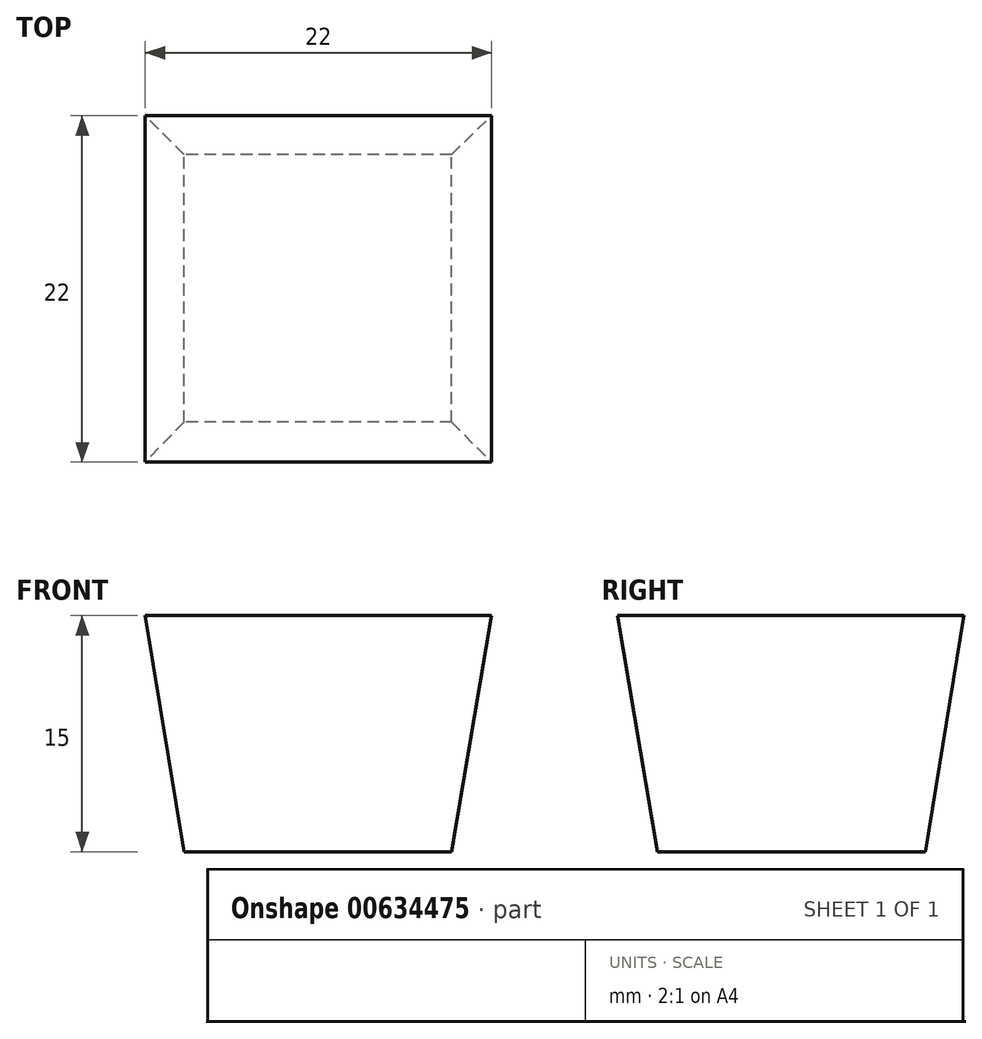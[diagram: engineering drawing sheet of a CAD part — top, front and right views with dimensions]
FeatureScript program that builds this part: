
annotation { "Feature Type Name" : "Feature", "Feature Type Description" : "" }
export const myFeature = defineFeature(function(context is Context, id is Id, definition is map)
    precondition{}
    {
        {
            var Q0;
            Q0=qCreatedBy(makeId("Top.planeOp"),FACE);
            var sketch = newSketch(context, id + "F0", { "sketchPlane" : qUnion([Q0])});
            skLineSegment(sketch, "E0.bottom", {"start": v(0, 0) * mm, "end": v(-17, 0) * mm});
            skLineSegment(sketch, "E0.top", {"start": v(0, 17) * mm, "end": v(-17, 17) * mm});
            skLineSegment(sketch, "E0.left", {"start": v(0, 0) * mm, "end": v(0, 17) * mm});
            skLineSegment(sketch, "E0.right", {"start": v(-17, 0) * mm, "end": v(-17, 17) * mm});
            skSolve(sketch);
        }
        {
            var Q0;
            Q0=qCreatedBy(makeId("Top.planeOp"),FACE);
            cPlane(context, id + "F1", {"entities" : qUnion([Q0]), "cplaneType" : CPlaneType.OFFSET, "offset" : 15 * mm, "width" : 152.4 * mm, "height" : 152.4 * mm});
        }
        {
            var Q0;
            Q0=qCreatedBy(id+"F1.planeOp",FACE);
            var sketch = newSketch(context, id + "F2", { "sketchPlane" : qUnion([Q0])});
            skLineSegment(sketch, "E1.bottom", {"start": v(2.54, -2.54) * mm, "end": v(-19.46, -2.54) * mm});
            skLineSegment(sketch, "E1.top", {"start": v(2.54, 19.46) * mm, "end": v(-19.46, 19.46) * mm});
            skLineSegment(sketch, "E1.left", {"start": v(2.54, -2.54) * mm, "end": v(2.54, 19.46) * mm});
            skLineSegment(sketch, "E1.right", {"start": v(-19.46, -2.54) * mm, "end": v(-19.46, 19.46) * mm});
            skSolve(sketch);
        }
        {
            var Q0;
            Q0 = qSketchRegion(id + "F0", true);
            var Q1;
            Q1 = qSketchRegion(id + "F2", true);
            loft(context, id + "F3", {"sheetProfilesArray" : [{ "sheetProfileEntities" : qUnion([Q0]) }, { "sheetProfileEntities" : qUnion([Q1]) }]});
        }
    });
